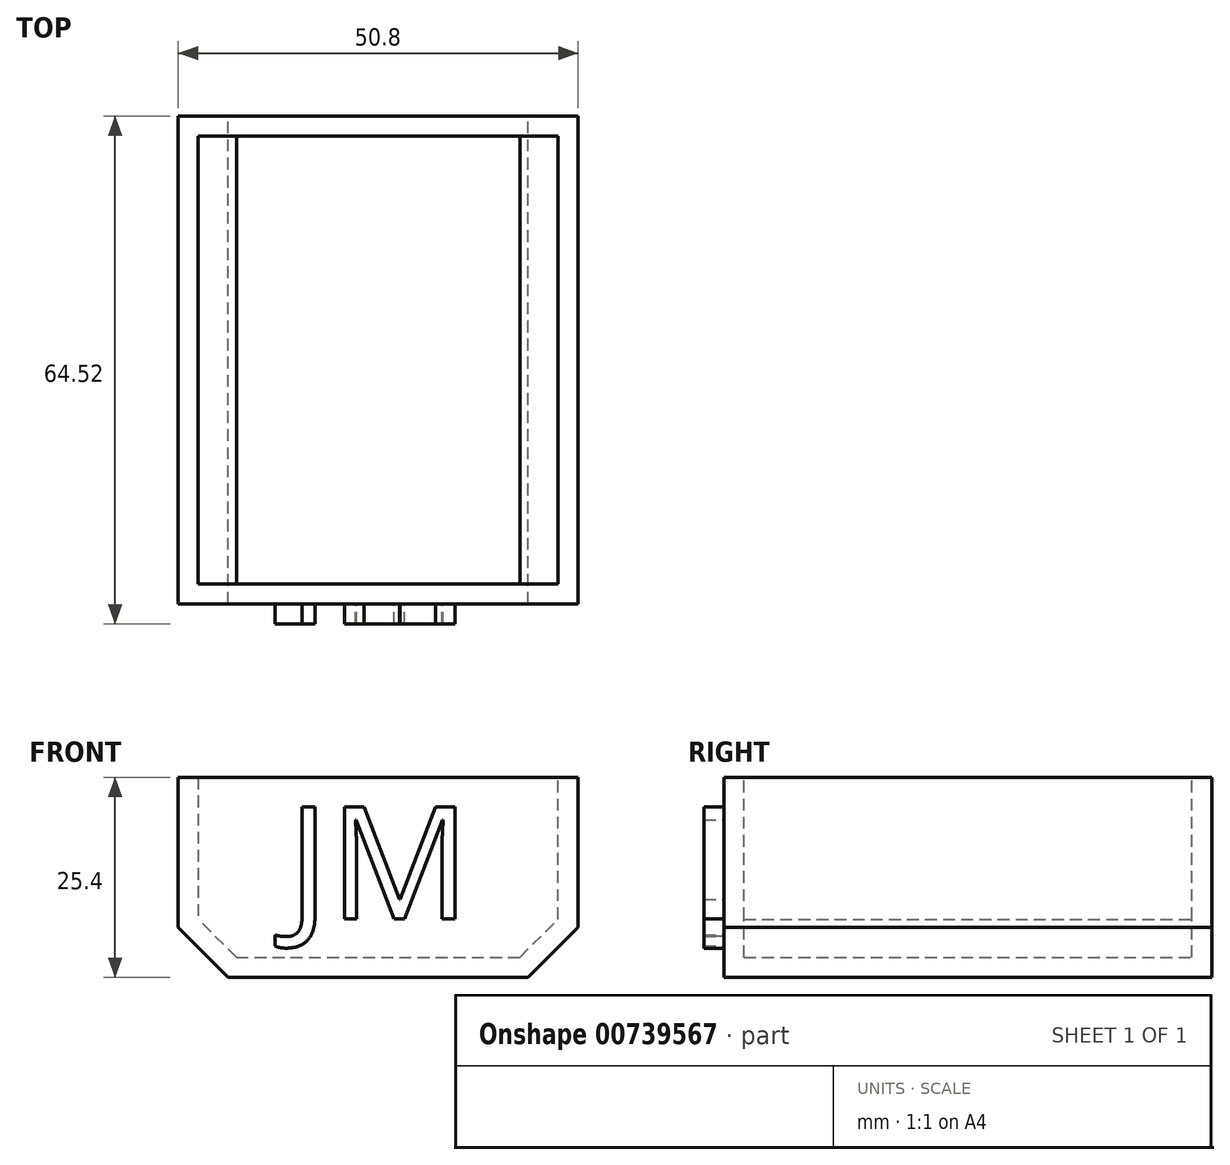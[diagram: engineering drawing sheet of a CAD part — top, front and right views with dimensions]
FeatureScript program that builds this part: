
annotation { "Feature Type Name" : "Feature", "Feature Type Description" : "" }
export const myFeature = defineFeature(function(context is Context, id is Id, definition is map)
    precondition{}
    {
        {
            var Q0;
            Q0=qCreatedBy(makeId("Front.planeOp"),FACE);
            var sketch = newSketch(context, id + "F0", { "sketchPlane" : qUnion([Q0])});
            skLineSegment(sketch, "E0", {"start": v(6.35, 0) * mm, "end": v(0, 6.35) * mm});
            skLineSegment(sketch, "E1", {"start": v(6.35, 0) * mm, "end": v(44.45, 0) * mm});
            skLineSegment(sketch, "E2", {"start": v(44.45, 0) * mm, "end": v(50.8, 6.35) * mm});
            skLineSegment(sketch, "E3", {"start": v(50.8, 6.35) * mm, "end": v(50.8, 25.4) * mm});
            skLineSegment(sketch, "E4", {"start": v(50.8, 25.4) * mm, "end": v(0, 25.4) * mm});
            skLineSegment(sketch, "E5", {"start": v(0, 25.4) * mm, "end": v(0, 6.35) * mm});
            skSolve(sketch);
        }
        {
            var Q0;
            Q0=makeQuery(id+"F0.imprint","IMPRINT",FACE,{"disambiguationData":[TD([[makeQuery(id+"F0.imprint","IMPRINT",EDGE,{"derivedFrom":sQuery(id+"F0.wireOp",EDGE,"E0")}),-1.0]])]});
            extrude(context, id + "F1", {"entities" : qUnion([Q0]), "depth" : 61.98 * mm, "offsetDistance" : 25.4 * mm});
        }
        {
            var Q0;
            Q0=makeQuery(id+"F1.opExtrude","SWEPT_FACE",FACE,{"disambiguationData":[OSD([sQuery(id+"F0.wireOp",EDGE,"E4")])]});
            shell(context, id + "F2", {"entities" : qUnion([Q0]), "thickness" : 2.54 * mm});
        }
        {
            var Q0;
            Q0=makeQuery(id+"F1.opExtrude","CAP_FACE",FACE,{"disambiguationData":[OSD([sQuery(id+"F0.wireOp",EDGE,"E0"),sQuery(id+"F0.wireOp",EDGE,"E1"),sQuery(id+"F0.wireOp",EDGE,"E2"),sQuery(id+"F0.wireOp",EDGE,"E3"),sQuery(id+"F0.wireOp",EDGE,"E4"),sQuery(id+"F0.wireOp",EDGE,"E5")])],"isStart":false});
            var sketch = newSketch(context, id + "F3", { "sketchPlane" : qUnion([Q0])});
            skText(sketch, "E6", { "text": "JM", "fontName": "OpenSans-Regular.ttf"});
            const initialGuessF3  = {"E6": [0.01387, 0.00745, 1, 0, 0.0143]};
            skSetInitialGuess(sketch, initialGuessF3);
            skSolve(sketch);
        }
        {
            var Q0;
            Q0 = qSketchRegion(id + "F3", true);
            extrude(context, id + "F4", {"entities" : qUnion([Q0]), "operationType" : NewBodyOperationType.ADD, "depth" : 2.54 * mm, "offsetDistance" : 25.4 * mm});
        }
    });
